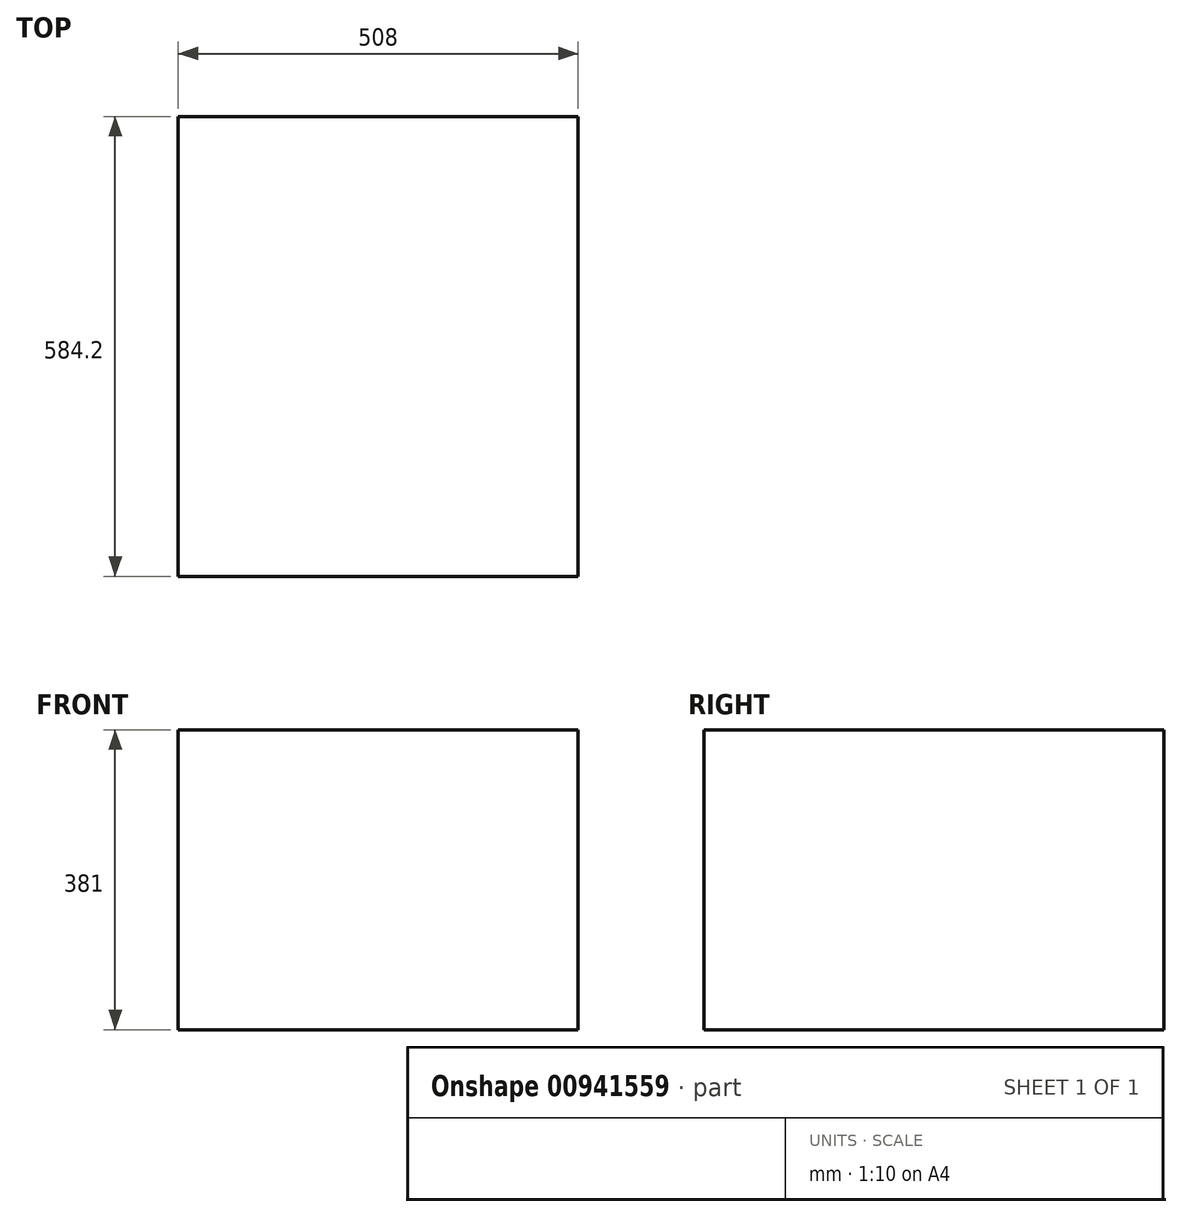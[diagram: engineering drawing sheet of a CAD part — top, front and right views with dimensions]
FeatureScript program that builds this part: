
annotation { "Feature Type Name" : "Feature", "Feature Type Description" : "" }
export const myFeature = defineFeature(function(context is Context, id is Id, definition is map)
    precondition{}
    {
        {
            var Q0;
            Q0=qCreatedBy(makeId("Front.planeOp"),FACE);
            var sketch = newSketch(context, id + "F0", { "sketchPlane" : qUnion([Q0])});
            skLineSegment(sketch, "E0.bottom", {"start": v(254, 190.5) * mm, "end": v(-254, 190.5) * mm});
            skLineSegment(sketch, "E0.top", {"start": v(254, -190.5) * mm, "end": v(-254, -190.5) * mm});
            skLineSegment(sketch, "E0.left", {"start": v(254, 190.5) * mm, "end": v(254, -190.5) * mm});
            skLineSegment(sketch, "E0.right", {"start": v(-254, 190.5) * mm, "end": v(-254, -190.5) * mm});
            skPoint(sketch, "E0.middle", {"position": v(0, 0) * mm});
            skSolve(sketch);
        }
        {
            var Q0;
            Q0 = qSketchRegion(id + "F0", true);
            extrude(context, id + "F1", {"entities" : qUnion([Q0]), "oppositeDirection" : true, "depth" : 584.2 * mm, "offsetDistance" : 25.4 * mm});
        }
    });
